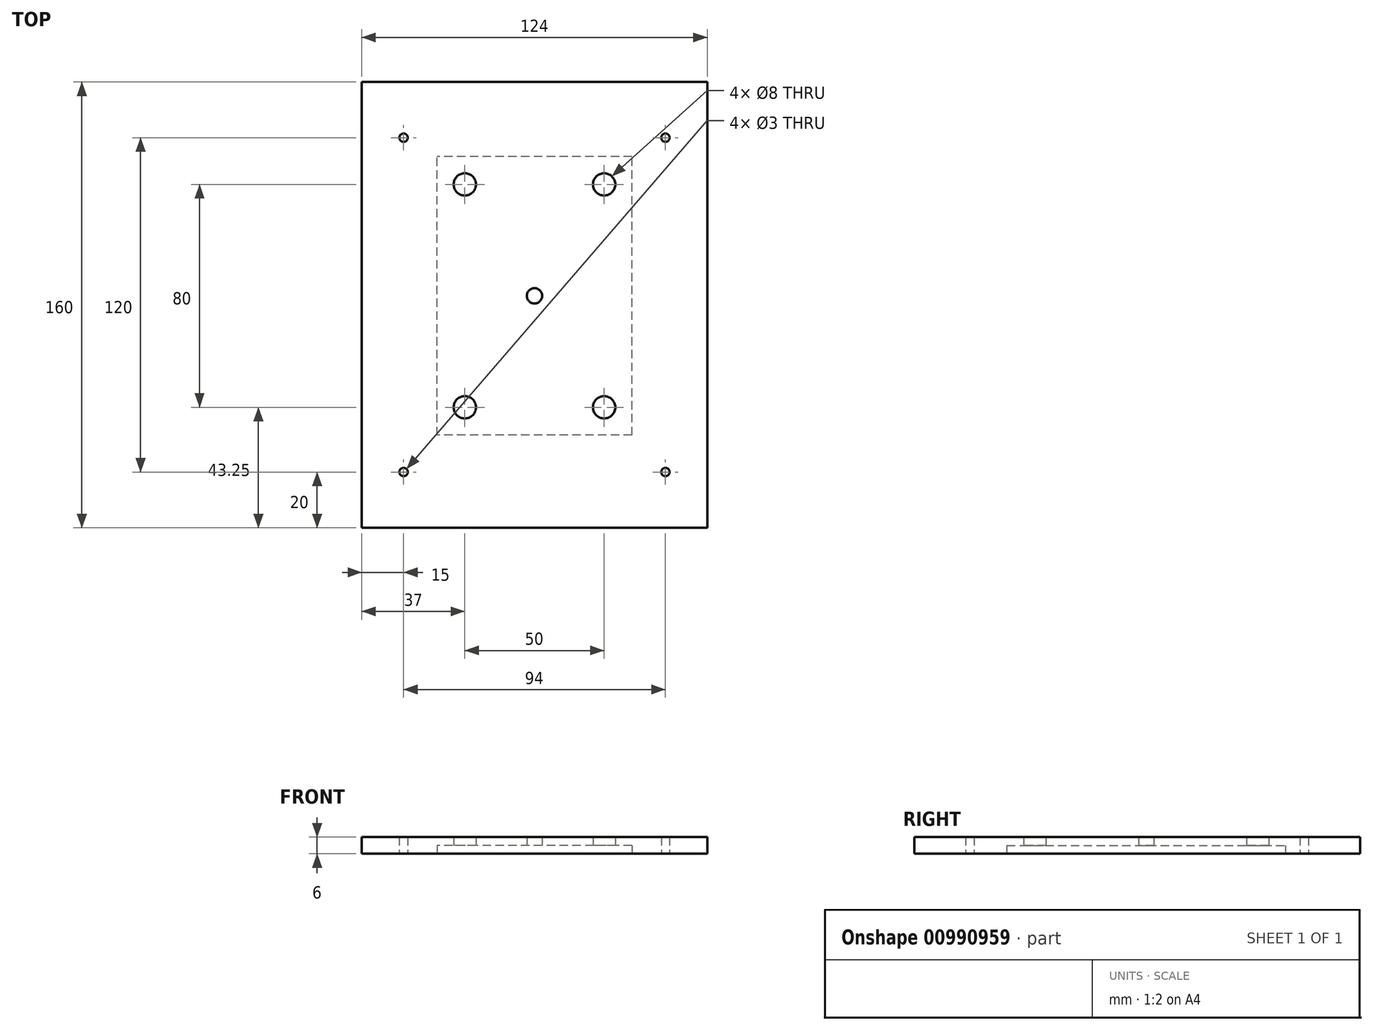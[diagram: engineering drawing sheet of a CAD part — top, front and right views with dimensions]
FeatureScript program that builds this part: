
annotation { "Feature Type Name" : "Feature", "Feature Type Description" : "" }
export const myFeature = defineFeature(function(context is Context, id is Id, definition is map)
    precondition{}
    {
        {
            var Q0;
            Q0=qCreatedBy(makeId("Top.planeOp"),FACE);
            var sketch = newSketch(context, id + "F0", { "sketchPlane" : qUnion([Q0])});
            skLineSegment(sketch, "E0.bottom", {"start": v(62, -79.75) * mm, "end": v(-62, -79.75) * mm});
            skLineSegment(sketch, "E0.top", {"start": v(62, 80.25) * mm, "end": v(-62, 80.25) * mm});
            skLineSegment(sketch, "E0.left", {"start": v(62, -79.75) * mm, "end": v(62, 80.25) * mm});
            skLineSegment(sketch, "E0.right", {"start": v(-62, -79.75) * mm, "end": v(-62, 80.25) * mm});
            skPoint(sketch, "E0.middle", {"position": v(0, 3.5) * mm});
            skLineSegment(sketch, "E1", {"start": v(0, 80.25) * mm, "end": v(0, -79.75) * mm, "construction": true});
            skCircle(sketch, "E2", {"center": v(-47, 60.25) * mm, "radius": 1.5 * mm});
            skCircle(sketch, "E3.MirrorC", {"center": v(47, 60.25) * mm, "radius": 1.5 * mm});
            skCircle(sketch, "E4", {"center": v(-47, -59.75) * mm, "radius": 1.5 * mm});
            skCircle(sketch, "E5.MirrorC", {"center": v(47, -59.75) * mm, "radius": 1.5 * mm});
            skLineSegment(sketch, "E6.bottom", {"start": v(35, -46.5) * mm, "end": v(-35, -46.5) * mm});
            skLineSegment(sketch, "E6.top", {"start": v(35, 53.5) * mm, "end": v(-35, 53.5) * mm});
            skLineSegment(sketch, "E6.left", {"start": v(35, -46.5) * mm, "end": v(35, 53.5) * mm});
            skLineSegment(sketch, "E6.right", {"start": v(-35, -46.5) * mm, "end": v(-35, 53.5) * mm});
            skCircle(sketch, "E7", {"center": v(-25, 43.5) * mm, "radius": 4 * mm});
            skCircle(sketch, "E8.MirrorC", {"center": v(25, 43.5) * mm, "radius": 4 * mm});
            skCircle(sketch, "E9.MirrorC", {"center": v(-25, -36.5) * mm, "radius": 4 * mm});
            skCircle(sketch, "E10.MirrorC", {"center": v(25, -36.5) * mm, "radius": 4 * mm});
            skCircle(sketch, "E11", {"center": v(0, 3.5) * mm, "radius": 2.75 * mm});
            skSolve(sketch);
        }
        {
            var Q0;
            Q0 = qSketchRegion(id + "F0", true);
            var Q1;
            Q1=makeQuery(id+"F0.imprint","IMPRINT",FACE,{"disambiguationData":[TD([[makeQuery(id+"F0.imprint","IMPRINT",EDGE,{"derivedFrom":sQuery(id+"F0.wireOp",EDGE,"E6.bottom")}),-1.0]])]});
            extrude(context, id + "F1", {"entities" : qUnion([Q0, Q1]), "depth" : 6 * mm, "offsetDistance" : 25 * mm});
        }
        {
            var Q0;
            Q0=makeQuery(id+"F0.imprint","IMPRINT",FACE,{"disambiguationData":[TD([[makeQuery(id+"F0.imprint","IMPRINT",EDGE,{"derivedFrom":sQuery(id+"F0.wireOp",EDGE,"E6.bottom")}),-1.0]])]});
            extrude(context, id + "F2", {"entities" : qUnion([Q0]), "operationType" : NewBodyOperationType.REMOVE, "depth" : 3 * mm, "offsetDistance" : 25 * mm});
        }
    });
